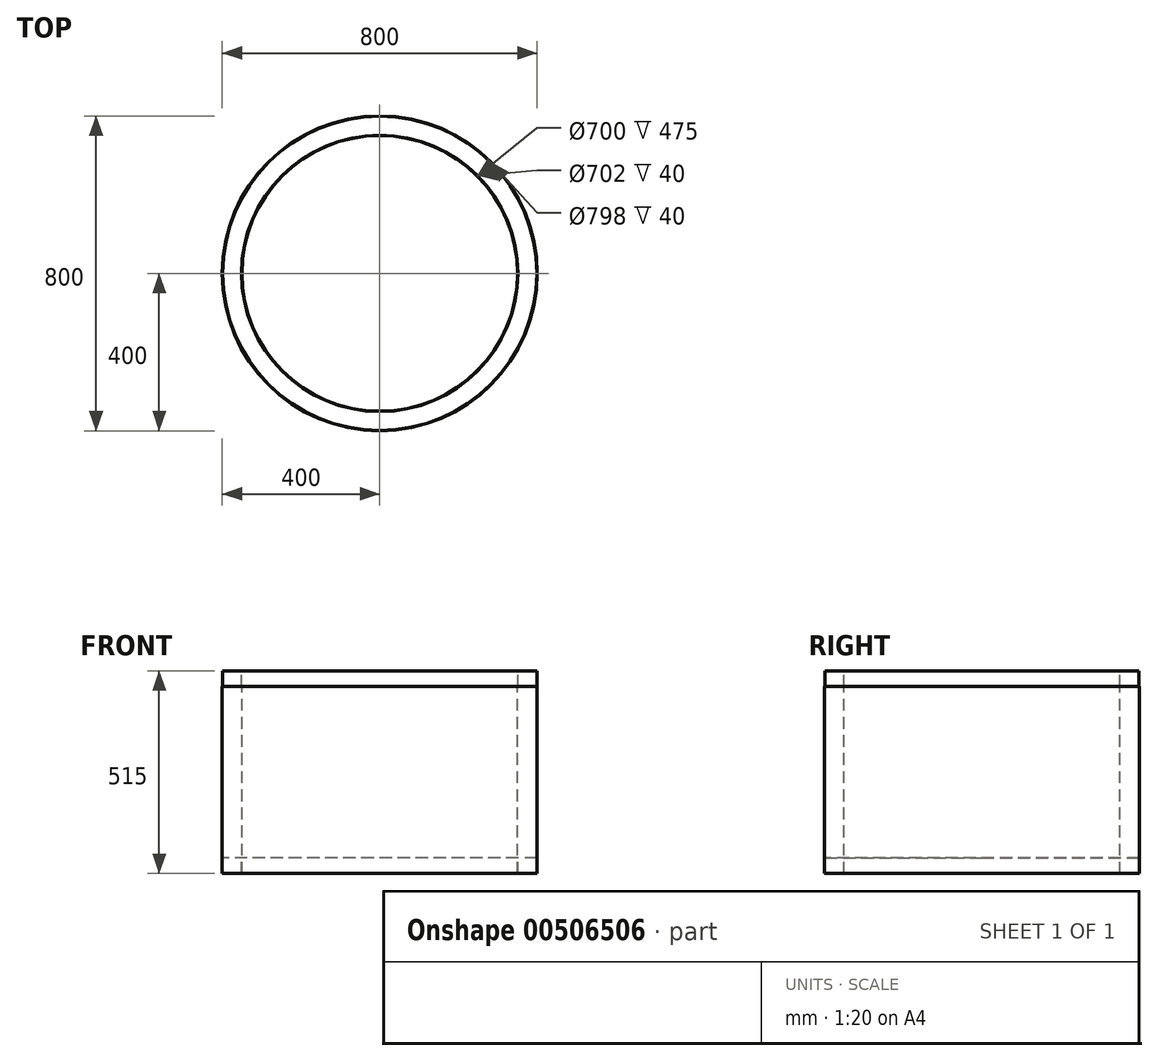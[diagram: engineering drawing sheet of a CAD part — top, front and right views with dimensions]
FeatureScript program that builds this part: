
annotation { "Feature Type Name" : "Feature", "Feature Type Description" : "" }
export const myFeature = defineFeature(function(context is Context, id is Id, definition is map)
    precondition{}
    {
        {
            var Q0;
            Q0=qCreatedBy(makeId("Front.planeOp"),FACE);
            var sketch = newSketch(context, id + "F0", { "sketchPlane" : qUnion([Q0])});
            skLineSegment(sketch, "E0", {"start": v(0, 74.87) * mm, "end": v(0, -73.71) * mm, "construction": true});
            skLineSegment(sketch, "E1", {"start": v(0, 374.84) * mm, "end": v(0, -528.94) * mm, "construction": true});
            skLineSegment(sketch, "E2", {"start": v(-350, -489.75) * mm, "end": v(-350, -14.75) * mm});
            skLineSegment(sketch, "E3", {"start": v(-350, -14.75) * mm, "end": v(-351, -14.75) * mm});
            skLineSegment(sketch, "E4", {"start": v(-351, -14.75) * mm, "end": v(-351, 25.25) * mm});
            skLineSegment(sketch, "E5", {"start": v(-351, 25.25) * mm, "end": v(-399, 25.25) * mm});
            skLineSegment(sketch, "E6", {"start": v(-399, 25.25) * mm, "end": v(-399, -14.75) * mm});
            skLineSegment(sketch, "E7", {"start": v(-399, -14.75) * mm, "end": v(-400, -14.75) * mm});
            skLineSegment(sketch, "E8", {"start": v(-400, -14.75) * mm, "end": v(-400, -489.75) * mm});
            skLineSegment(sketch, "E9", {"start": v(-400, -489.75) * mm, "end": v(-399, -489.75) * mm});
            skLineSegment(sketch, "E10", {"start": v(-399, -489.75) * mm, "end": v(-399, -449.75) * mm});
            skLineSegment(sketch, "E11", {"start": v(-399, -449.75) * mm, "end": v(-351, -449.75) * mm});
            skLineSegment(sketch, "E12", {"start": v(-351, -449.75) * mm, "end": v(-351, -489.75) * mm});
            skLineSegment(sketch, "E13", {"start": v(-351, -489.75) * mm, "end": v(-350, -489.75) * mm});
            skSolve(sketch);
        }
        {
            var Q0;
            Q0=qSketchRegion(id+"F0",true);
            var Q1;
            Q1=sQuery(id+"F0.wireOp",EDGE,"E1");
            revolve(context, id + "F1", {"entities" : qUnion([Q0]), "axis" : qUnion([Q1]), "revolveType" : RevolveType.FULL});
        }
    });
